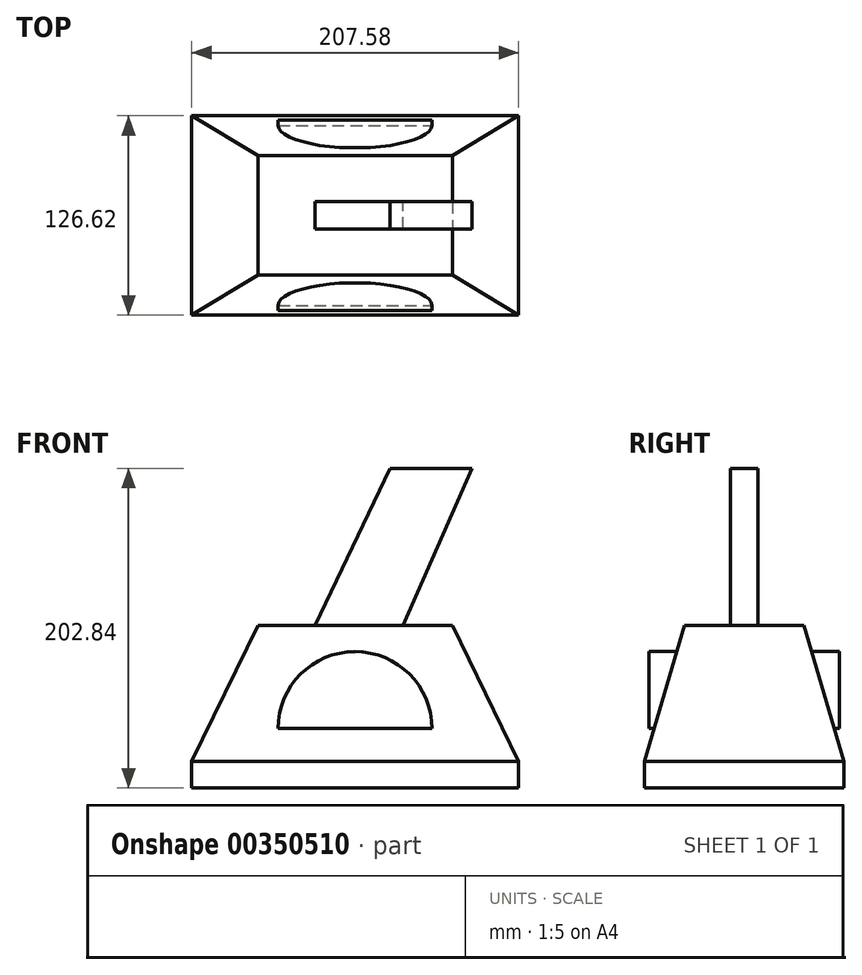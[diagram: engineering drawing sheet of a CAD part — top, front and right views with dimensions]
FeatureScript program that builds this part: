
annotation { "Feature Type Name" : "Feature", "Feature Type Description" : "" }
export const myFeature = defineFeature(function(context is Context, id is Id, definition is map)
    precondition{}
    {
        {
            var Q0;
            Q0=qCreatedBy(makeId("Top.planeOp"),FACE);
            cPlane(context, id + "F0", {"entities" : qUnion([Q0]), "cplaneType" : CPlaneType.OFFSET, "offset" : 86.36 * mm, "width" : 152.4 * mm, "height" : 152.4 * mm});
        }
        {
            var Q0;
            Q0=qCreatedBy(makeId("Top.planeOp"),FACE);
            var sketch = newSketch(context, id + "F1", { "sketchPlane" : qUnion([Q0])});
            skLineSegment(sketch, "E0.bottom", {"start": v(103.8, 63.3) * mm, "end": v(-103.8, 63.3) * mm});
            skLineSegment(sketch, "E0.top", {"start": v(103.8, -63.3) * mm, "end": v(-103.8, -63.3) * mm});
            skLineSegment(sketch, "E0.left", {"start": v(103.8, 63.3) * mm, "end": v(103.8, -63.3) * mm});
            skLineSegment(sketch, "E0.right", {"start": v(-103.8, 63.3) * mm, "end": v(-103.8, -63.3) * mm});
            skPoint(sketch, "E0.middle", {"position": v(0, 0) * mm});
            skSolve(sketch);
        }
        {
            var Q0;
            Q0=qCreatedBy(id+"F0.planeOp",FACE);
            var sketch = newSketch(context, id + "F2", { "sketchPlane" : qUnion([Q0])});
            skLineSegment(sketch, "E1.bottom", {"start": v(61.73, 37.92) * mm, "end": v(-61.73, 37.92) * mm});
            skLineSegment(sketch, "E1.top", {"start": v(61.73, -37.92) * mm, "end": v(-61.73, -37.92) * mm});
            skLineSegment(sketch, "E1.left", {"start": v(61.73, 37.92) * mm, "end": v(61.73, -37.92) * mm});
            skLineSegment(sketch, "E1.right", {"start": v(-61.73, 37.92) * mm, "end": v(-61.73, -37.92) * mm});
            skPoint(sketch, "E1.middle", {"position": v(0, 0) * mm});
            skSolve(sketch);
        }
        {
            var Q0;
            Q0=makeQuery(id+"F1.imprint","IMPRINT",FACE,{"disambiguationData":[TD([[makeQuery(id+"F1.imprint","IMPRINT",EDGE,{"derivedFrom":sQuery(id+"F1.wireOp",EDGE,"E0.bottom")}),1.0]])]});
            var Q1;
            Q1=makeQuery(id+"F2.imprint","IMPRINT",FACE,{"disambiguationData":[TD([[makeQuery(id+"F2.imprint","IMPRINT",EDGE,{"derivedFrom":sQuery(id+"F2.wireOp",EDGE,"E1.bottom")}),1.0]])]});
            loft(context, id + "F3", {"sheetProfilesArray" : [{ "sheetProfileEntities" : qUnion([Q0]) }, { "sheetProfileEntities" : qUnion([Q1]) }]});
        }
        {
            var Q0;
            Q0=qCreatedBy(makeId("Front.planeOp"),FACE);
            var sketch = newSketch(context, id + "F4", { "sketchPlane" : qUnion([Q0])});
            skArc(sketch, "E2", {"start": v(48.88, 20.88) * mm, "mid": v(0, 69.76) * mm, "end": v(-48.88, 20.88) * mm});
            skLineSegment(sketch, "E3", {"start": v(-48.88, 20.88) * mm, "end": v(48.88, 20.88) * mm});
            skLineSegment(sketch, "E4", {"start": v(-26.02, 84.85) * mm, "end": v(22.33, 186.08) * mm});
            skLineSegment(sketch, "E5", {"start": v(22.33, 186.08) * mm, "end": v(74.2, 186.08) * mm});
            skLineSegment(sketch, "E6", {"start": v(74.2, 186.08) * mm, "end": v(28.37, 81.32) * mm});
            skLineSegment(sketch, "E7", {"start": v(28.37, 81.32) * mm, "end": v(-29.04, 81.32) * mm});
            skLineSegment(sketch, "E8", {"start": v(-29.04, 81.32) * mm, "end": v(-26.02, 84.85) * mm});
            skSolve(sketch);
        }
        {
            var Q0;
            Q0=makeQuery(id+"F4.imprint","IMPRINT",FACE,{"disambiguationData":[TD([[makeQuery(id+"F4.imprint","IMPRINT",EDGE,{"derivedFrom":sQuery(id+"F4.wireOp",EDGE,"E2")}),1.0]])]});
            extrude(context, id + "F5", {"entities" : qUnion([Q0]), "operationType" : NewBodyOperationType.ADD, "endBound" : BoundingType.SYMMETRIC, "depth" : 120.9 * mm});
        }
        {
            var Q0;
            Q0=makeQuery(id+"F3.opLoft","CAP_FACE",FACE,{"disambiguationData":[OSD([makeQuery(id+"F1.imprint","IMPRINT",FACE,{"disambiguationData":[TD([[makeQuery(id+"F1.imprint","IMPRINT",EDGE,{"derivedFrom":sQuery(id+"F1.wireOp",EDGE,"E0.bottom")}),1.0]])]})])],"isStart":true});
            var sketch = newSketch(context, id + "F6", { "sketchPlane" : qUnion([Q0])});
            skLineSegment(sketch, "E9.bottom", {"start": v(-103.8, 63.3) * mm, "end": v(103.8, 63.3) * mm});
            skLineSegment(sketch, "E9.top", {"start": v(-103.8, -63.3) * mm, "end": v(103.8, -63.3) * mm});
            skLineSegment(sketch, "E9.left", {"start": v(-103.8, 63.3) * mm, "end": v(-103.8, -63.3) * mm});
            skLineSegment(sketch, "E9.right", {"start": v(103.8, 63.3) * mm, "end": v(103.8, -63.3) * mm});
            skSolve(sketch);
        }
        {
            var Q0;
            Q0=makeQuery(id+"F6.imprint","IMPRINT",FACE,{"disambiguationData":[TD([[makeQuery(id+"F6.imprint","IMPRINT",EDGE,{"derivedFrom":sQuery(id+"F6.wireOp",EDGE,"E9.bottom")}),-1.0]])]});
            extrude(context, id + "F7", {"entities" : qUnion([Q0]), "operationType" : NewBodyOperationType.ADD, "depth" : 16.76 * mm});
        }
        {
            var Q0;
            Q0=makeQuery(id+"F4.imprint","IMPRINT",FACE,{"disambiguationData":[TD([[makeQuery(id+"F4.imprint","IMPRINT",EDGE,{"derivedFrom":sQuery(id+"F4.wireOp",EDGE,"E4")}),-1.0]])]});
            extrude(context, id + "F8", {"entities" : qUnion([Q0]), "operationType" : NewBodyOperationType.ADD, "endBound" : BoundingType.SYMMETRIC, "depth" : 17.27 * mm});
        }
    });
